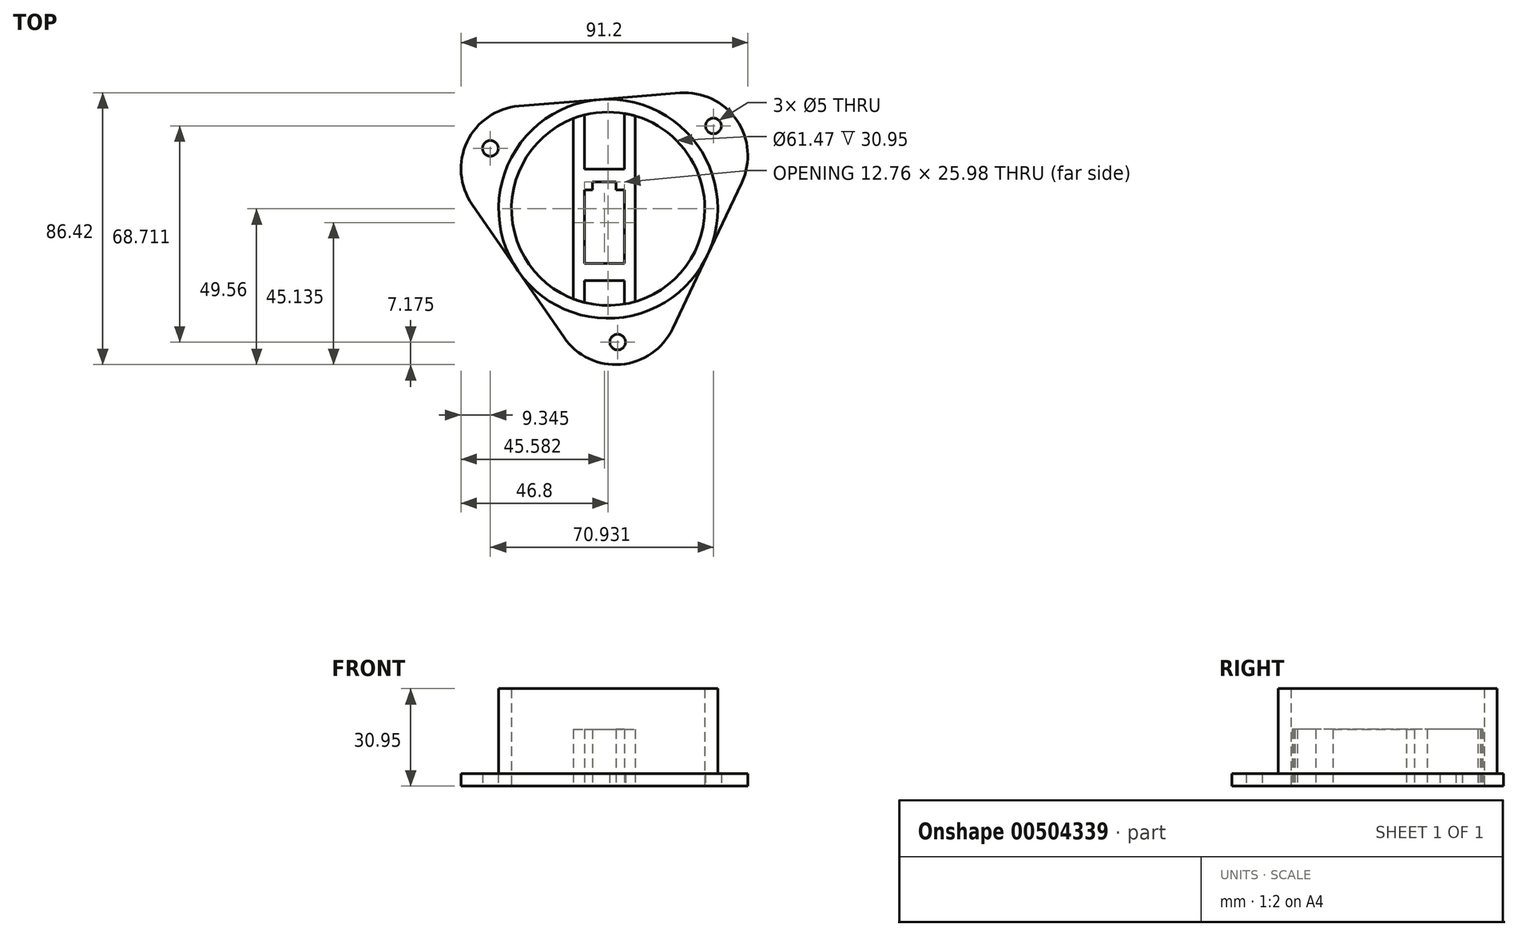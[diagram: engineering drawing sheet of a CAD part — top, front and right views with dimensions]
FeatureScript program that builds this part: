
annotation { "Feature Type Name" : "Feature", "Feature Type Description" : "" }
export const myFeature = defineFeature(function(context is Context, id is Id, definition is map)
    precondition{}
    {
        {
            var Q0;
            Q0=qCreatedBy(makeId("Top.planeOp"),FACE);
            var sketch = newSketch(context, id + "F0", { "sketchPlane" : qUnion([Q0])});
            skCircle(sketch, "E0", {"center": v(0, 0) * mm, "radius": 34.83 * mm});
            skCircle(sketch, "E1", {"center": v(0, 0) * mm, "radius": 30.73 * mm});
            skLineSegment(sketch, "E2.left", {"start": v(-11.05, 28.68) * mm, "end": v(-11.05, -28.68) * mm});
            skLineSegment(sketch, "E2.right", {"start": v(8.61, 28.68) * mm, "end": v(8.61, -29.5) * mm});
            skLineSegment(sketch, "E3", {"start": v(5.16, 30.3) * mm, "end": v(5.16, 12.6) * mm});
            skLineSegment(sketch, "E4", {"start": v(-7.6, 29.78) * mm, "end": v(-7.6, 12.6) * mm});
            skLineSegment(sketch, "E5", {"start": v(-7.6, -22.84) * mm, "end": v(5.16, -22.83) * mm});
            skLineSegment(sketch, "E6", {"start": v(-7.6, -17.41) * mm, "end": v(5.16, -17.41) * mm});
            skLineSegment(sketch, "E7", {"start": v(5.16, -17.41) * mm, "end": v(5.16, 5.94) * mm});
            skLineSegment(sketch, "E8", {"start": v(5.16, 5.94) * mm, "end": v(2.53, 5.94) * mm});
            skLineSegment(sketch, "E9", {"start": v(-7.6, 5.94) * mm, "end": v(-4.97, 5.94) * mm});
            skLineSegment(sketch, "E10", {"start": v(2.53, 5.94) * mm, "end": v(2.53, 8.57) * mm});
            skLineSegment(sketch, "E11", {"start": v(-4.97, 5.94) * mm, "end": v(-4.97, 8.57) * mm});
            skLineSegment(sketch, "E12", {"start": v(-4.97, 8.57) * mm, "end": v(2.53, 8.57) * mm});
            skLineSegment(sketch, "E13", {"start": v(-7.6, 12.6) * mm, "end": v(5.16, 12.6) * mm});
            skLineSegment(sketch, "E14.trimOffspring", {"start": v(5.16, 5.94) * mm, "end": v(5.16, -17.41) * mm});
            skLineSegment(sketch, "E15.trimOffspring", {"start": v(-7.6, 5.94) * mm, "end": v(-7.6, -17.41) * mm});
            skLineSegment(sketch, "E16.trimOffspring", {"start": v(-7.6, -22.84) * mm, "end": v(-7.6, -29.78) * mm});
            skLineSegment(sketch, "E17.trimOffspring", {"start": v(5.16, -22.83) * mm, "end": v(5.16, -30.3) * mm});
            skLineSegment(sketch, "E18", {"start": v(8.61, 28.68) * mm, "end": v(8.61, 29.5) * mm});
            skCircle(sketch, "E19.cCircle", {"center": v(0, 0) * mm, "radius": 34.83 * mm, "construction": true});
            skLineSegment(sketch, "E19.0", {"start": v(42.48, 8.29) * mm, "end": v(20.47, -38.13) * mm});
            skLineSegment(sketch, "E19.1", {"start": v(-14.06, -40.93) * mm, "end": v(-43.26, 1.34) * mm});
            skLineSegment(sketch, "E19.2", {"start": v(-28.42, 32.64) * mm, "end": v(22.79, 36.8) * mm});
            skPoint(sketch, "E19.0.midPoint", {"position": v(31.47, -14.92) * mm});
            skPoint(sketch, "E20.visualSharp", {"position": v(5.63, -69.43) * mm});
            skArc(sketch, "E20.filletArc", {"start": v(-14.06, -40.93) * mm, "mid": v(4.01, -49.5) * mm, "end": v(20.47, -38.13) * mm});
            skPoint(sketch, "E21.visualSharp", {"position": v(-62.94, 29.84) * mm});
            skArc(sketch, "E21.filletArc", {"start": v(-28.42, 32.64) * mm, "mid": v(-44.87, 21.27) * mm, "end": v(-43.26, 1.34) * mm});
            skPoint(sketch, "E22.visualSharp", {"position": v(57.32, 39.59) * mm});
            skArc(sketch, "E22.filletArc", {"start": v(42.48, 8.29) * mm, "mid": v(40.86, 28.22) * mm, "end": v(22.79, 36.8) * mm});
            skSolve(sketch);
        }
        {
            var Q0;
            Q0=makeQuery(id+"F0.imprint","IMPRINT",FACE,{"disambiguationData":[TD([[makeQuery(id+"F0.imprint","IMPRINT",EDGE,{"derivedFrom":sQuery(id+"F0.wireOp",EDGE,"E0")}),1.0]])]});
            extrude(context, id + "F1", {"entities" : qUnion([Q0]), "depth" : 30.95 * mm});
        }
        {
            var Q0;
            {var subQ2=sQuery(id+"F0.wireOp",EDGE,"E2.left");Q0=makeQuery(id+"F0.imprint","IMPRINT",FACE,{"disambiguationData":[TD([[makeQuery(id+"F0.imprint","IMPRINT",EDGE,{"derivedFrom":subQ2}),1.0]])]});}
            extrude(context, id + "F2", {"entities" : qUnion([Q0]), "operationType" : NewBodyOperationType.ADD, "depth" : 18 * mm});
        }
        {
            var Q0;
            Q0=qCreatedBy(makeId("Top.planeOp"),FACE);
            var sketch = newSketch(context, id + "F3", { "sketchPlane" : qUnion([Q0])});
            skCircle(sketch, "E23", {"center": v(-37.46, 19.19) * mm, "radius": 2.5 * mm});
            skCircle(sketch, "E24", {"center": v(33.48, 26.33) * mm, "radius": 2.5 * mm});
            skCircle(sketch, "E25", {"center": v(3.02, -42.38) * mm, "radius": 2.5 * mm});
            skSolve(sketch);
        }
        {
            var Q0;
            {var subQ5=sQuery(id+"F0.wireOp",EDGE,"E21.filletArc");Q0=makeQuery(id+"F0.imprint","IMPRINT",FACE,{"disambiguationData":[TD([[makeQuery(id+"F0.imprint","IMPRINT",EDGE,{"derivedFrom":subQ5}),1.0]])]});}
            var Q1;
            {var subQ5=sQuery(id+"F0.wireOp",EDGE,"E22.filletArc");Q1=makeQuery(id+"F0.imprint","IMPRINT",FACE,{"disambiguationData":[TD([[makeQuery(id+"F0.imprint","IMPRINT",EDGE,{"derivedFrom":subQ5}),1.0]])]});}
            extrude(context, id + "F4", {"entities" : qUnion([Q0, Q1]), "operationType" : NewBodyOperationType.ADD, "depth" : 4 * mm, "offsetDistance" : 25 * mm});
        }
        {
            var Q0;
            {var subQ5=sQuery(id+"F0.wireOp",EDGE,"E20.filletArc");Q0=makeQuery(id+"F0.imprint","IMPRINT",FACE,{"disambiguationData":[TD([[makeQuery(id+"F0.imprint","IMPRINT",EDGE,{"derivedFrom":subQ5}),1.0]])]});}
            extrude(context, id + "F5", {"entities" : qUnion([Q0]), "operationType" : NewBodyOperationType.ADD, "depth" : 4 * mm, "offsetDistance" : 25 * mm});
        }
        {
            var Q0;
            Q0=sQuery(id+"F3.wireOp",VERTEX,"E23.center");
            var Q1;
            Q1=sQuery(id+"F3.wireOp",VERTEX,"E24.center");
            var Q2;
            Q2=sQuery(id+"F3.wireOp",VERTEX,"E25.center");
            var Q3;
            Q3=makeQuery(id+"F1.opExtrude","SWEPT_BODY",BODY,{"disambiguationData":[OSD([sQuery(id+"F0.wireOp",EDGE,"E0"),sQuery(id+"F0.wireOp",EDGE,"E1")])]});
            hole(context, id + "F6", {"style" : HoleStyle.SIMPLE, "endStyle" : HoleEndStyle.THROUGH, "oppositeDirection" : true, "holeDiameter" : 5 * mm, "isTappedThrough" : true, "tappedDepth" : 12 * mm, "tapClearance" : 3, "locations" : qUnion([Q0, Q1, Q2]), "scope" : qUnion([Q3])});
        }
    });
